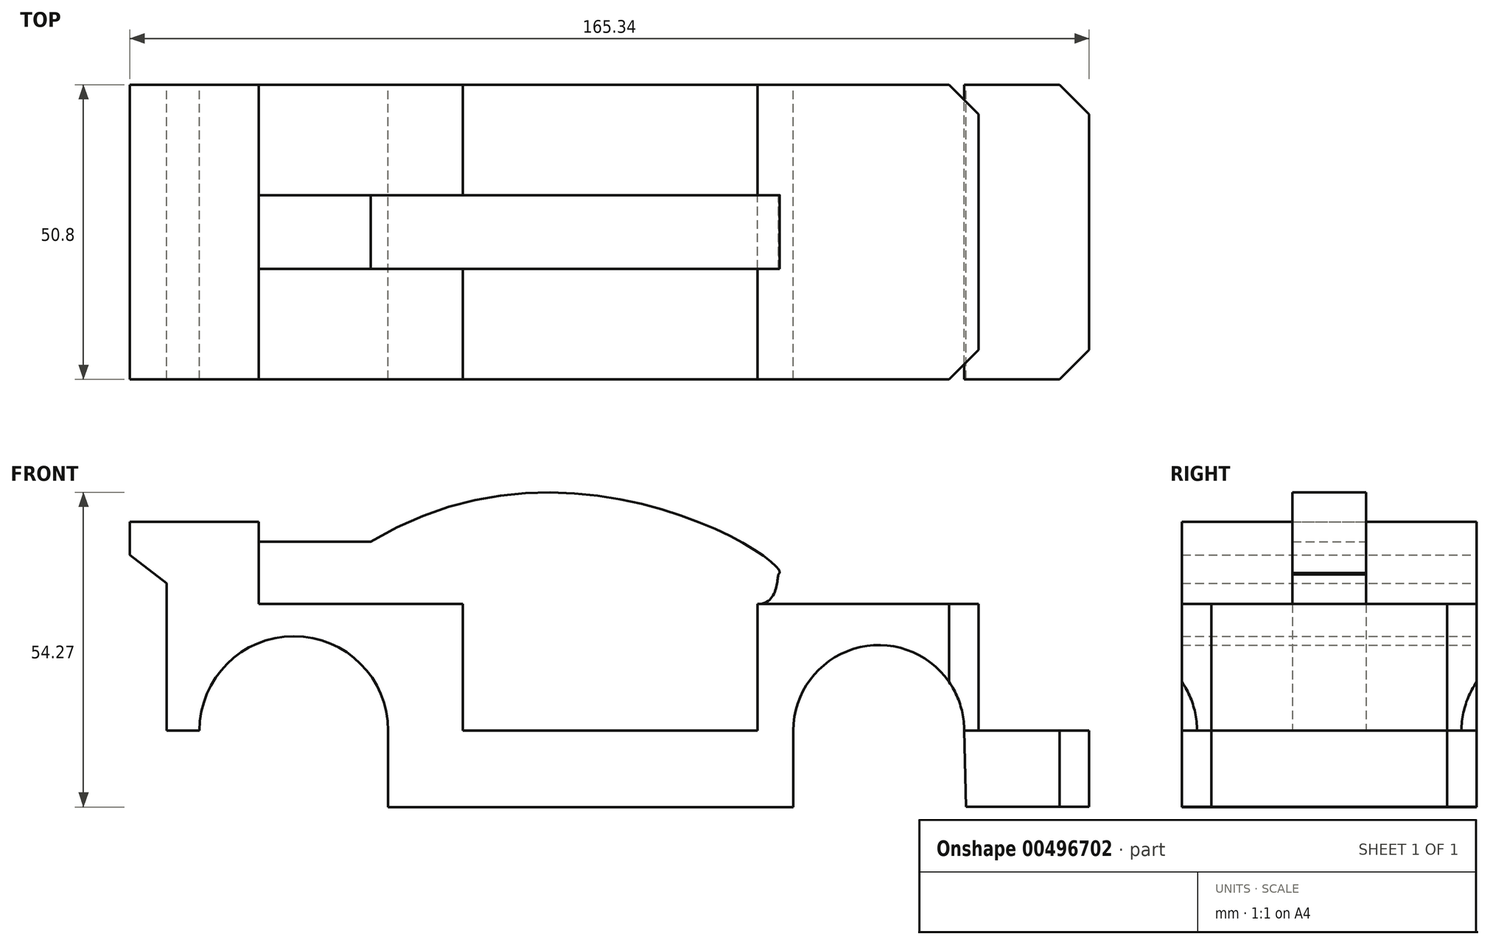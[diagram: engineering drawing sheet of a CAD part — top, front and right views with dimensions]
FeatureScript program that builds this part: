
annotation { "Feature Type Name" : "Feature", "Feature Type Description" : "" }
export const myFeature = defineFeature(function(context is Context, id is Id, definition is map)
    precondition{}
    {
        {
            var Q0;
            Q0=qCreatedBy(makeId("Front.planeOp"),FACE);
            var sketch = newSketch(context, id + "F0", { "sketchPlane" : qUnion([Q0])});
            skLineSegment(sketch, "E0", {"start": v(-97.35, 36) * mm, "end": v(-75.13, 36) * mm});
            skLineSegment(sketch, "E1", {"start": v(-97.35, 36) * mm, "end": v(-97.35, 30.27) * mm});
            skLineSegment(sketch, "E2", {"start": v(-97.35, 30.27) * mm, "end": v(-91.02, 25.4) * mm});
            skLineSegment(sketch, "E3", {"start": v(-91.02, 25.4) * mm, "end": v(-91.02, 0) * mm});
            skLineSegment(sketch, "E4", {"start": v(-75.13, 36) * mm, "end": v(-75.13, 21.82) * mm});
            skLineSegment(sketch, "E5", {"start": v(-75.13, 21.82) * mm, "end": v(-39.96, 21.82) * mm});
            skLineSegment(sketch, "E6", {"start": v(-39.96, 21.82) * mm, "end": v(-39.96, 0) * mm});
            skLineSegment(sketch, "E7", {"start": v(-39.96, 0) * mm, "end": v(10.84, 0) * mm});
            skLineSegment(sketch, "E8", {"start": v(10.84, 0) * mm, "end": v(10.84, 21.82) * mm});
            skLineSegment(sketch, "E9", {"start": v(10.84, 21.82) * mm, "end": v(48.94, 21.82) * mm});
            skLineSegment(sketch, "E10", {"start": v(48.94, 21.82) * mm, "end": v(48.94, 0) * mm});
            skLineSegment(sketch, "E11", {"start": v(48.94, 0) * mm, "end": v(67.99, 0) * mm});
            skLineSegment(sketch, "E12", {"start": v(67.99, 0) * mm, "end": v(67.99, 0) * mm});
            skLineSegment(sketch, "E13", {"start": v(67.99, 0) * mm, "end": v(67.99, -13.19) * mm});
            skLineSegment(sketch, "E14", {"start": v(67.99, -13.19) * mm, "end": v(48.94, -13.19) * mm});
            skLineSegment(sketch, "E15", {"start": v(-91.02, 0) * mm, "end": v(-85.36, 0) * mm});
            skLineSegment(sketch, "E16", {"start": v(-39.96, 0) * mm, "end": v(-52.83, 0) * mm});
            skLineSegment(sketch, "E17", {"start": v(-52.83, 0) * mm, "end": v(-52.83, -13.2) * mm});
            skLineSegment(sketch, "E18.bottom", {"start": v(-75.13, 32.56) * mm, "end": v(-55.84, 32.56) * mm});
            skLineSegment(sketch, "E18.left", {"start": v(-75.13, 32.56) * mm, "end": v(-75.13, 21.82) * mm});
            skLineSegment(sketch, "E19", {"start": v(-55.84, 32.56) * mm, "end": v(-55.84, 21.82) * mm});
            skLineSegment(sketch, "E20", {"start": v(-39.96, 21.82) * mm, "end": v(-55.84, 21.82) * mm});
            skFitSpline(sketch, "E21", {"points": [v(10.84, 21.82) * mm, v(14.44, 26.89) * mm, v(14.64, 27.22) * mm, v(14.58, 27.36) * mm], "startDerivative": vector(14.83, 0) * mm, "endDerivative": vector(-2.2, -0.36) * mm});
            skFitSpline(sketch, "E22", {"points": [v(-55.84, 32.56) * mm, v(14.66, 27.38) * mm, v(14.44, 26.89) * mm], "startDerivative": vector(110.4, 66.94) * mm, "endDerivative": vector(0.22, -4.23) * mm});
            skLineSegment(sketch, "E23", {"start": v(-52.83, -13.2) * mm, "end": v(17.02, -13.2) * mm});
            skLineSegment(sketch, "E24", {"start": v(48.94, 0) * mm, "end": v(48.94, -13.19) * mm});
            skLineSegment(sketch, "E25", {"start": v(-55.84, 21.82) * mm, "end": v(10.84, 21.82) * mm});
            skLineSegment(sketch, "E26", {"start": v(17.02, -13.2) * mm, "end": v(17.02, 0) * mm});
            skLineSegment(sketch, "E27", {"start": v(59.29, 0) * mm, "end": v(48.94, 0) * mm});
            skArc(sketch, "E28", {"start": v(46.46, 0) * mm, "mid": v(31.74, 14.72) * mm, "end": v(17.02, 0) * mm});
            skLineSegment(sketch, "E29", {"start": v(46.46, 0) * mm, "end": v(48.94, 0) * mm});
            skArc(sketch, "E30", {"start": v(-52.83, 0) * mm, "mid": v(-69.1, 16.27) * mm, "end": v(-85.36, 0) * mm});
            skLineSegment(sketch, "E31", {"start": v(48.94, -13.19) * mm, "end": v(46.77, -13.19) * mm});
            skLineSegment(sketch, "E32", {"start": v(46.77, -13.19) * mm, "end": v(46.46, 0) * mm});
            skSolve(sketch);
        }
        {
            var Q0;
            Q0=makeQuery(id+"F0.imprint","IMPRINT",FACE,{"disambiguationData":[TD([[makeQuery(id+"F0.imprint","IMPRINT",EDGE,{"derivedFrom":sQuery(id+"F0.wireOp",EDGE,"E0")}),-1.0]])]});
            extrude(context, id + "F1", {"entities" : qUnion([Q0]), "endBound" : BoundingType.SYMMETRIC, "depth" : 50.8 * mm});
        }
        {
            var Q0;
            Q0=makeQuery(id+"F0.imprint","IMPRINT",FACE,{"disambiguationData":[TD([[makeQuery(id+"F0.imprint","IMPRINT",EDGE,{"derivedFrom":sQuery(id+"F0.wireOp",EDGE,"E18.bottom")}),-1.0]])]});
            extrude(context, id + "F2", {"entities" : qUnion([Q0]), "operationType" : NewBodyOperationType.ADD, "endBound" : BoundingType.SYMMETRIC, "depth" : 12.7 * mm});
        }
        {
            var Q0;
            Q0=makeQuery(id+"F0.imprint","IMPRINT",FACE,{"disambiguationData":[TD([[makeQuery(id+"F0.imprint","IMPRINT",EDGE,{"derivedFrom":sQuery(id+"F0.wireOp",EDGE,"E6")}),1.0]])]});
            extrude(context, id + "F3", {"entities" : qUnion([Q0]), "operationType" : NewBodyOperationType.ADD, "endBound" : BoundingType.SYMMETRIC, "depth" : 12.7 * mm});
        }
        {
            var Q0;
            Q0=makeQuery(id+"F0.imprint","IMPRINT",FACE,{"disambiguationData":[TD([[makeQuery(id+"F0.imprint","IMPRINT",EDGE,{"derivedFrom":sQuery(id+"F0.wireOp",EDGE,"E7")}),-1.0]])]});
            extrude(context, id + "F4", {"entities" : qUnion([Q0]), "operationType" : NewBodyOperationType.ADD, "endBound" : BoundingType.SYMMETRIC, "depth" : 50.8 * mm});
        }
        {
            var Q0;
            {var subQ1=sQuery(id+"F0.wireOp",EDGE,"E19");Q0=makeQuery(id+"F0.imprint","IMPRINT",FACE,{"disambiguationData":[TD([[makeQuery(id+"F0.imprint","IMPRINT",EDGE,{"derivedFrom":subQ1}),1.0]])]});}
            extrude(context, id + "F5", {"entities" : qUnion([Q0]), "operationType" : NewBodyOperationType.ADD, "endBound" : BoundingType.SYMMETRIC, "depth" : 12.7 * mm});
        }
        {
            var Q0;
            Q0=makeQuery(id+"F4.boolean.opBoolean","MERGE",FACE,{"derivedFrom":[makeQuery(id+"F3.opExtrude","SWEPT_FACE",FACE,{"disambiguationData":[OSD([sQuery(id+"F0.wireOp",EDGE,"E20"),sQuery(id+"F0.wireOp",EDGE,"E25")])]}),makeQuery(id+"F4.opExtrude","SWEPT_FACE",FACE,{"disambiguationData":[OSD([sQuery(id+"F0.wireOp",EDGE,"E9")])]})]});
            var sketch = newSketch(context, id + "F6", { "sketchPlane" : qUnion([Q0])});
            skLineSegment(sketch, "E33", {"start": v(48.94, -20.85) * mm, "end": v(39.85, -25.4) * mm});
            skLineSegment(sketch, "E34", {"start": v(48.94, 20.85) * mm, "end": v(39.85, 25.4) * mm});
            skLineSegment(sketch, "E35", {"start": v(39.85, 25.4) * mm, "end": v(48.94, 25.4) * mm});
            skLineSegment(sketch, "E36", {"start": v(48.94, 25.4) * mm, "end": v(48.94, 20.85) * mm});
            skLineSegment(sketch, "E37", {"start": v(48.94, -20.85) * mm, "end": v(48.94, -25.4) * mm});
            skLineSegment(sketch, "E38", {"start": v(48.94, -25.4) * mm, "end": v(39.85, -25.4) * mm});
            skSolve(sketch);
        }
        {
            var Q0;
            Q0=makeQuery(id+"F0.imprint","IMPRINT",FACE,{"disambiguationData":[TD([[makeQuery(id+"F0.imprint","IMPRINT",EDGE,{"derivedFrom":sQuery(id+"F0.wireOp",EDGE,"E24")}),-1.0]])]});
            var Q1;
            Q1=makeQuery(id+"F0.imprint","IMPRINT",FACE,{"disambiguationData":[TD([[makeQuery(id+"F0.imprint","IMPRINT",EDGE,{"derivedFrom":sQuery(id+"F0.wireOp",EDGE,"E11")}),-1.0]])]});
            extrude(context, id + "F7", {"entities" : qUnion([Q0, Q1]), "operationType" : NewBodyOperationType.ADD, "endBound" : BoundingType.SYMMETRIC, "depth" : 50.8 * mm});
        }
        {
            var Q0;
            Q0=makeQuery(id+"F7.opExtrude","CAP_EDGE",EDGE,{"disambiguationData":[OSD([sQuery(id+"F0.wireOp",EDGE,"E13")])],"isStart":false});
            var Q1;
            Q1=makeQuery(id+"F7.opExtrude","CAP_EDGE",EDGE,{"disambiguationData":[OSD([sQuery(id+"F0.wireOp",EDGE,"E13")])],"isStart":true});
            chamfer(context, id + "F8", {"entities" : qUnion([Q0, Q1]), "width" : 5.08 * mm, "tangentPropagation" : true});
        }
        {
            var Q0;
            Q0=makeQuery(id+"F4.opExtrude","CAP_EDGE",EDGE,{"disambiguationData":[OSD([sQuery(id+"F0.wireOp",EDGE,"E10")])],"isStart":false});
            var Q1;
            Q1=makeQuery(id+"F4.opExtrude","CAP_EDGE",EDGE,{"disambiguationData":[OSD([sQuery(id+"F0.wireOp",EDGE,"E10")])],"isStart":true});
            chamfer(context, id + "F9", {"entities" : qUnion([Q0, Q1]), "width" : 5.08 * mm, "tangentPropagation" : true});
        }
    });
